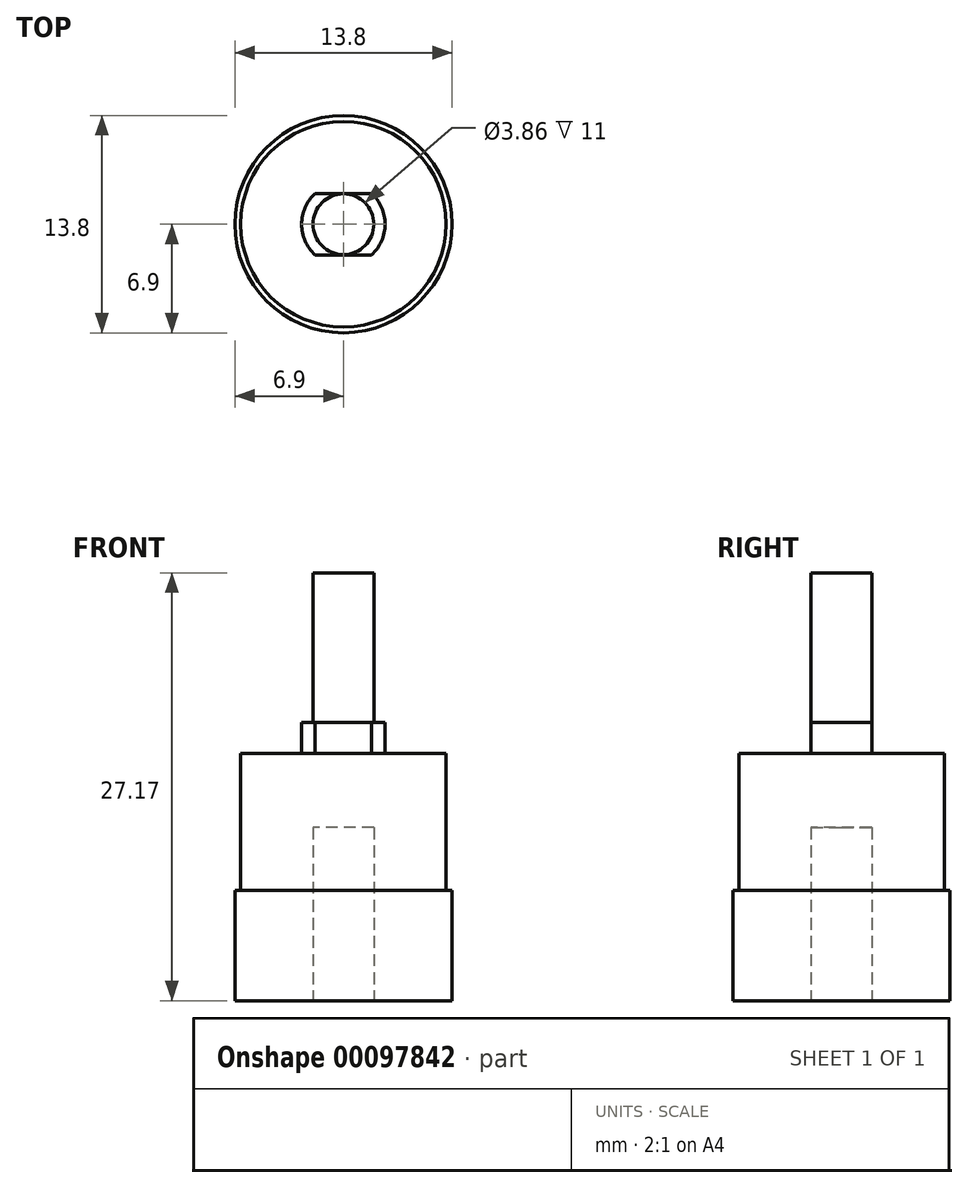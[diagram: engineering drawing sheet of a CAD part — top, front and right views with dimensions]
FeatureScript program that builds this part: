
annotation { "Feature Type Name" : "Feature", "Feature Type Description" : "" }
export const myFeature = defineFeature(function(context is Context, id is Id, definition is map)
    precondition{}
    {
        {
            var Q0;
            Q0=qCreatedBy(makeId("Top.planeOp"),FACE);
            var sketch = newSketch(context, id + "F0", { "sketchPlane" : qUnion([Q0])});
            skCircle(sketch, "E0", {"center": v(0, 0) * mm, "radius": 6.9 * mm});
            skCircle(sketch, "E1", {"center": v(0, 0) * mm, "radius": 6.53 * mm});
            skCircle(sketch, "E2", {"center": v(0, 0) * mm, "radius": 2.65 * mm});
            skLineSegment(sketch, "E3", {"start": v(-1.8, 1.95) * mm, "end": v(1.8, 1.95) * mm});
            skLineSegment(sketch, "E4", {"start": v(-1.8, -1.95) * mm, "end": v(1.8, -1.95) * mm});
            skLineSegment(sketch, "E5", {"start": v(-2.65, 0) * mm, "end": v(2.65, 0) * mm, "construction": true});
            skCircle(sketch, "E6", {"center": v(0, 0) * mm, "radius": 1.93 * mm});
            skSolve(sketch);
        }
        {
            var Q0;
            Q0=makeQuery(id+"F0.imprint","IMPRINT",FACE,{"disambiguationData":[TD([[makeQuery(id+"F0.imprint","IMPRINT",EDGE,{"derivedFrom":sQuery(id+"F0.wireOp",EDGE,"E6")}),1.0]])]});
            extrude(context, id + "F1", {"entities" : qUnion([Q0]), "depth" : 27.17 * mm, "hasSecondDirection" : true, "secondDirectionOppositeDirection" : false, "secondDirectionDepth" : 11 * mm});
        }
        {
            var Q0;
            {var subQ1=sQuery(id+"F0.wireOp",EDGE,"E3");Q0=makeQuery(id+"F0.imprint","IMPRINT",FACE,{"disambiguationData":[TD([[makeQuery(id+"F0.imprint","IMPRINT",EDGE,{"derivedFrom":subQ1}),-1.0]])]});}
            extrude(context, id + "F2", {"entities" : qUnion([Q0]), "operationType" : NewBodyOperationType.ADD, "depth" : 17.68 * mm});
        }
        {
            var Q0;
            {var subQ0=sQuery(id+"F0.wireOp",EDGE,"E4");Q0=makeQuery(id+"F0.imprint","IMPRINT",FACE,{"disambiguationData":[TD([[makeQuery(id+"F0.imprint","IMPRINT",EDGE,{"derivedFrom":subQ0}),-1.0]])]});}
            var Q1;
            {var subQ0=sQuery(id+"F0.wireOp",EDGE,"E3");Q1=makeQuery(id+"F0.imprint","IMPRINT",FACE,{"disambiguationData":[TD([[makeQuery(id+"F0.imprint","IMPRINT",EDGE,{"derivedFrom":subQ0}),1.0]])]});}
            var Q2;
            Q2=makeQuery(id+"F0.imprint","IMPRINT",FACE,{"disambiguationData":[TD([[makeQuery(id+"F0.imprint","IMPRINT",EDGE,{"derivedFrom":sQuery(id+"F0.wireOp",EDGE,"E1")}),1.0]])]});
            extrude(context, id + "F3", {"entities" : qUnion([Q0, Q1, Q2]), "operationType" : NewBodyOperationType.ADD, "depth" : 15.7 * mm});
        }
        {
            var Q0;
            Q0=makeQuery(id+"F0.imprint","IMPRINT",FACE,{"disambiguationData":[TD([[makeQuery(id+"F0.imprint","IMPRINT",EDGE,{"derivedFrom":sQuery(id+"F0.wireOp",EDGE,"E0")}),1.0]])]});
            extrude(context, id + "F4", {"entities" : qUnion([Q0]), "operationType" : NewBodyOperationType.ADD, "depth" : 7 * mm});
        }
    });
